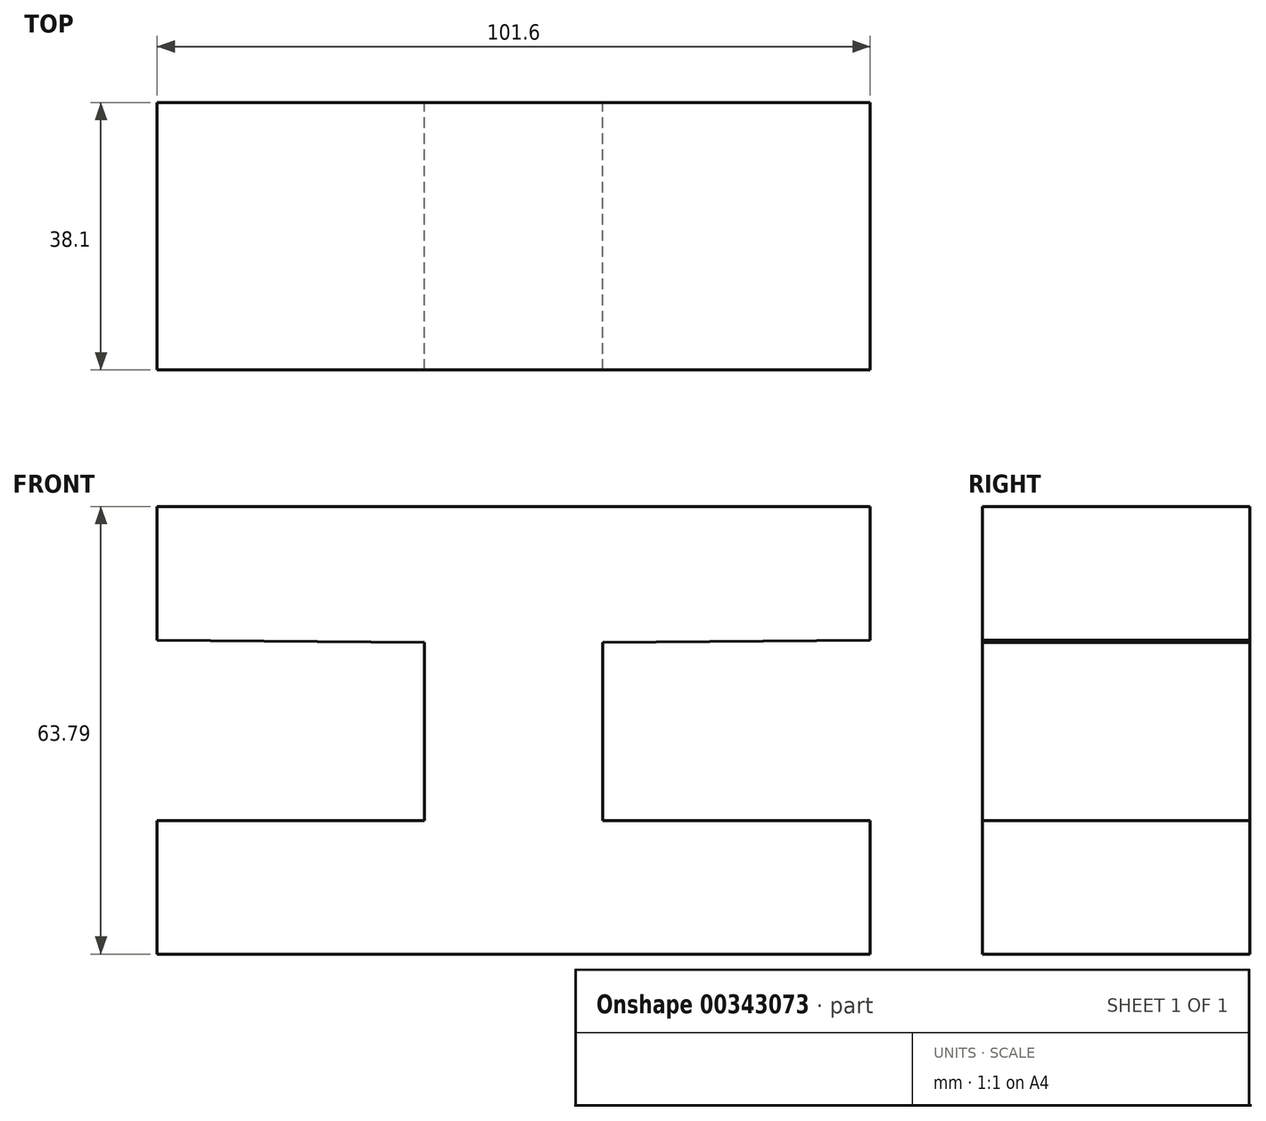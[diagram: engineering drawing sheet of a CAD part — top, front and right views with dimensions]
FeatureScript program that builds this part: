
annotation { "Feature Type Name" : "Feature", "Feature Type Description" : "" }
export const myFeature = defineFeature(function(context is Context, id is Id, definition is map)
    precondition{}
    {
        {
            var Q0;
            Q0=qCreatedBy(makeId("Front.planeOp"),FACE);
            var sketch = newSketch(context, id + "F0", { "sketchPlane" : qUnion([Q0])});
            skLineSegment(sketch, "E0", {"start": v(-32.94, -44.74) * mm, "end": v(68.66, -44.74) * mm});
            skLineSegment(sketch, "E1", {"start": v(68.66, -44.74) * mm, "end": v(68.66, -25.69) * mm});
            skLineSegment(sketch, "E2", {"start": v(68.66, -25.69) * mm, "end": v(30.56, -25.69) * mm});
            skLineSegment(sketch, "E3", {"start": v(-32.94, -44.74) * mm, "end": v(-32.94, -25.69) * mm});
            skLineSegment(sketch, "E4", {"start": v(-32.94, -25.69) * mm, "end": v(5.16, -25.69) * mm});
            skLineSegment(sketch, "E5", {"start": v(5.16, -25.69) * mm, "end": v(5.16, -0.29) * mm});
            skLineSegment(sketch, "E6", {"start": v(5.16, -0.29) * mm, "end": v(-32.94, 0) * mm});
            skLineSegment(sketch, "E7", {"start": v(-32.94, 0) * mm, "end": v(-32.94, 19.05) * mm});
            skLineSegment(sketch, "E8", {"start": v(-32.94, 19.05) * mm, "end": v(68.66, 19.05) * mm});
            skLineSegment(sketch, "E9", {"start": v(68.66, 19.05) * mm, "end": v(68.66, 0) * mm});
            skLineSegment(sketch, "E10", {"start": v(68.66, 0) * mm, "end": v(30.56, -0.29) * mm});
            skLineSegment(sketch, "E11", {"start": v(30.56, -0.29) * mm, "end": v(30.56, -25.69) * mm});
            skSolve(sketch);
        }
        {
            var Q0;
            Q0 = qSketchRegion(id + "F0", true);
            extrude(context, id + "F1", {"entities" : qUnion([Q0]), "depth" : 38.1 * mm});
        }
    });
